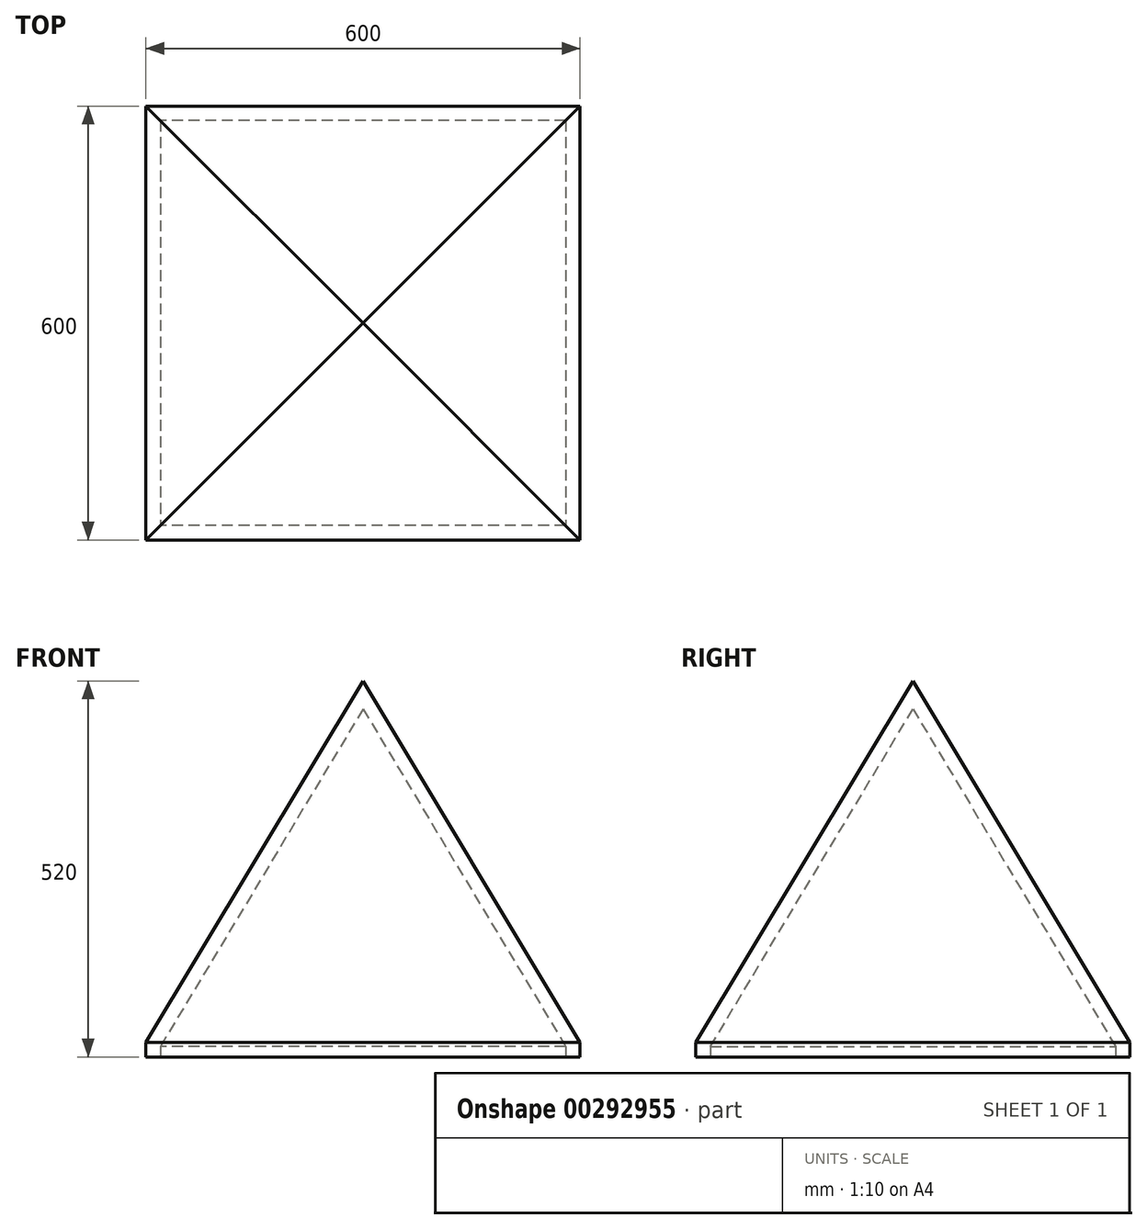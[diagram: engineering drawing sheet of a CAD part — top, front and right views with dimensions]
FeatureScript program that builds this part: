
annotation { "Feature Type Name" : "Feature", "Feature Type Description" : "" }
export const myFeature = defineFeature(function(context is Context, id is Id, definition is map)
    precondition{}
    {
        {
            var Q0;
            Q0=qCreatedBy(makeId("Top.planeOp"),FACE);
            var sketch = newSketch(context, id + "F0", { "sketchPlane" : qUnion([Q0])});
            skLineSegment(sketch, "E0.bottom", {"start": v(300, 300) * mm, "end": v(-300, 300) * mm});
            skLineSegment(sketch, "E0.top", {"start": v(300, -300) * mm, "end": v(-300, -300) * mm});
            skLineSegment(sketch, "E0.left", {"start": v(300, 300) * mm, "end": v(300, -300) * mm});
            skLineSegment(sketch, "E0.right", {"start": v(-300, 300) * mm, "end": v(-300, -300) * mm});
            skPoint(sketch, "E0.middle", {"position": v(0, 0) * mm});
            skSolve(sketch);
        }
        {
            var Q0;
            Q0 = qSketchRegion(id + "F0", true);
            extrude(context, id + "F1", {"entities" : qUnion([Q0]), "depth" : 20 * mm});
        }
        {
            var Q0;
            Q0=makeQuery(id+"F1.opExtrude","CAP_FACE",FACE,{"disambiguationData":[OSD([sQuery(id+"F0.wireOp",EDGE,"E0.bottom"),sQuery(id+"F0.wireOp",EDGE,"E0.top"),sQuery(id+"F0.wireOp",EDGE,"E0.left"),sQuery(id+"F0.wireOp",EDGE,"E0.right")])],"isStart":false});
            cPlane(context, id + "F2", {"entities" : qUnion([Q0]), "cplaneType" : CPlaneType.OFFSET, "offset" : 500 * mm, "width" : 150 * mm, "height" : 150 * mm});
        }
        {
            var Q0;
            Q0=qCreatedBy(id+"F2.planeOp",FACE);
            var sketch = newSketch(context, id + "F3", { "sketchPlane" : qUnion([Q0])});
            skPoint(sketch, "E1", {"position": v(0, 0) * mm});
            skSolve(sketch);
        }
        {
            var Q1;
            Q1=makeQuery(id+"F1.opExtrude","CAP_FACE",FACE,{"disambiguationData":[OSD([sQuery(id+"F0.wireOp",EDGE,"E0.bottom"),sQuery(id+"F0.wireOp",EDGE,"E0.top"),sQuery(id+"F0.wireOp",EDGE,"E0.left"),sQuery(id+"F0.wireOp",EDGE,"E0.right")])],"isStart":false});
            var Q2;
            Q2=sQuery(id+"F3.wireOp",VERTEX,"E1");
            loft(context, id + "F4", {"operationType" : NewBodyOperationType.ADD, "sheetProfilesArray" : [{ "sheetProfileEntities" : qUnion([Q1]) }, { "sheetProfileEntities" : qUnion([Q2]) }]});
        }
        {
            var Q0;
            Q0=makeQuery(id+"F1.opExtrude","CAP_FACE",FACE,{"disambiguationData":[OSD([sQuery(id+"F0.wireOp",EDGE,"E0.bottom"),sQuery(id+"F0.wireOp",EDGE,"E0.top"),sQuery(id+"F0.wireOp",EDGE,"E0.left"),sQuery(id+"F0.wireOp",EDGE,"E0.right")])],"isStart":true});
            shell(context, id + "F5", {"entities" : qUnion([Q0]), "thickness" : 20 * mm});
        }
    });
